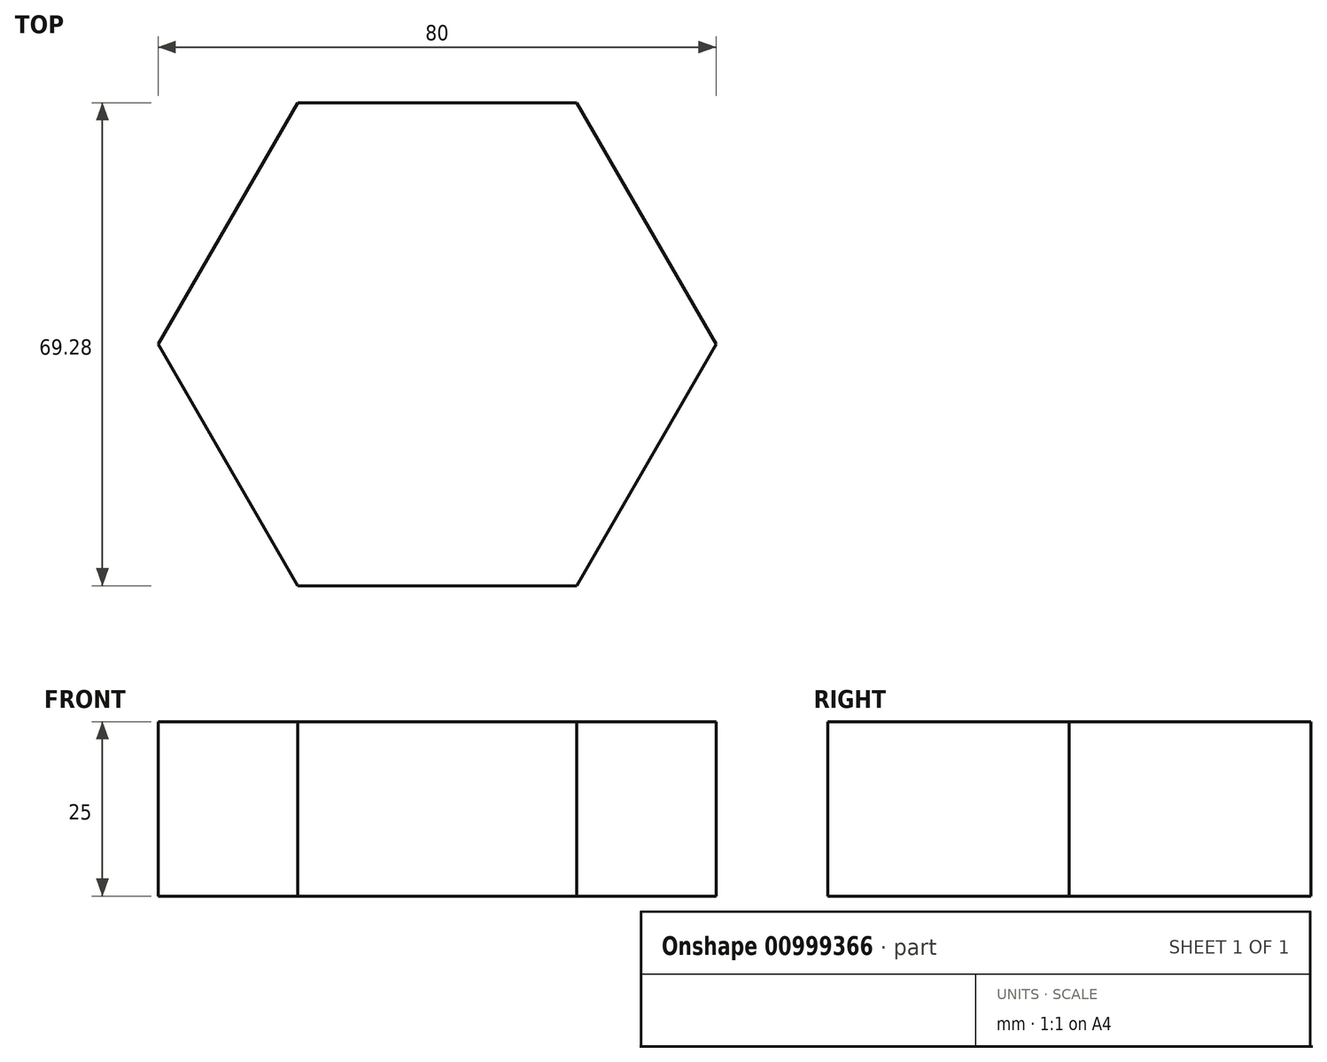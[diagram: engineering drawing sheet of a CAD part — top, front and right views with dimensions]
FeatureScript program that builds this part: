
annotation { "Feature Type Name" : "Feature", "Feature Type Description" : "" }
export const myFeature = defineFeature(function(context is Context, id is Id, definition is map)
    precondition{}
    {
        {
            var Q0;
            Q0=qCreatedBy(makeId("Top.planeOp"),FACE);
            var sketch = newSketch(context, id + "F0", { "sketchPlane" : qUnion([Q0])});
            skCircle(sketch, "E0", {"center": v(0, 0) * mm, "radius": 20 * mm});
            skCircle(sketch, "E1.cCircle", {"center": v(0, 0) * mm, "radius": 34.64 * mm, "construction": true});
            skLineSegment(sketch, "E1.0", {"start": v(-20, 34.64) * mm, "end": v(20, 34.64) * mm});
            skLineSegment(sketch, "E1.1", {"start": v(20, 34.64) * mm, "end": v(40, 0) * mm});
            skLineSegment(sketch, "E1.2", {"start": v(40, 0) * mm, "end": v(20, -34.64) * mm});
            skLineSegment(sketch, "E1.3", {"start": v(20, -34.64) * mm, "end": v(-20, -34.64) * mm});
            skLineSegment(sketch, "E1.4", {"start": v(-20, -34.64) * mm, "end": v(-40, 0) * mm});
            skLineSegment(sketch, "E1.5", {"start": v(-40, 0) * mm, "end": v(-20, 34.64) * mm});
            skPoint(sketch, "E1.0.midPoint", {"position": v(0, 34.64) * mm});
            skSolve(sketch);
        }
        {
            var Q0;
            Q0=makeQuery(id+"F0.imprint","IMPRINT",FACE,{"disambiguationData":[TD([[makeQuery(id+"F0.imprint","IMPRINT",EDGE,{"derivedFrom":sQuery(id+"F0.wireOp",EDGE,"E0")}),-1.0]])]});
            var Q1;
            Q1=makeQuery(id+"F0.imprint","IMPRINT",FACE,{"disambiguationData":[TD([[makeQuery(id+"F0.imprint","IMPRINT",EDGE,{"derivedFrom":sQuery(id+"F0.wireOp",EDGE,"E0")}),1.0]])]});
            extrude(context, id + "F1", {"entities" : qUnion([Q0, Q1]), "oppositeDirection" : true, "depth" : 25 * mm, "offsetDistance" : 25 * mm});
        }
    });
